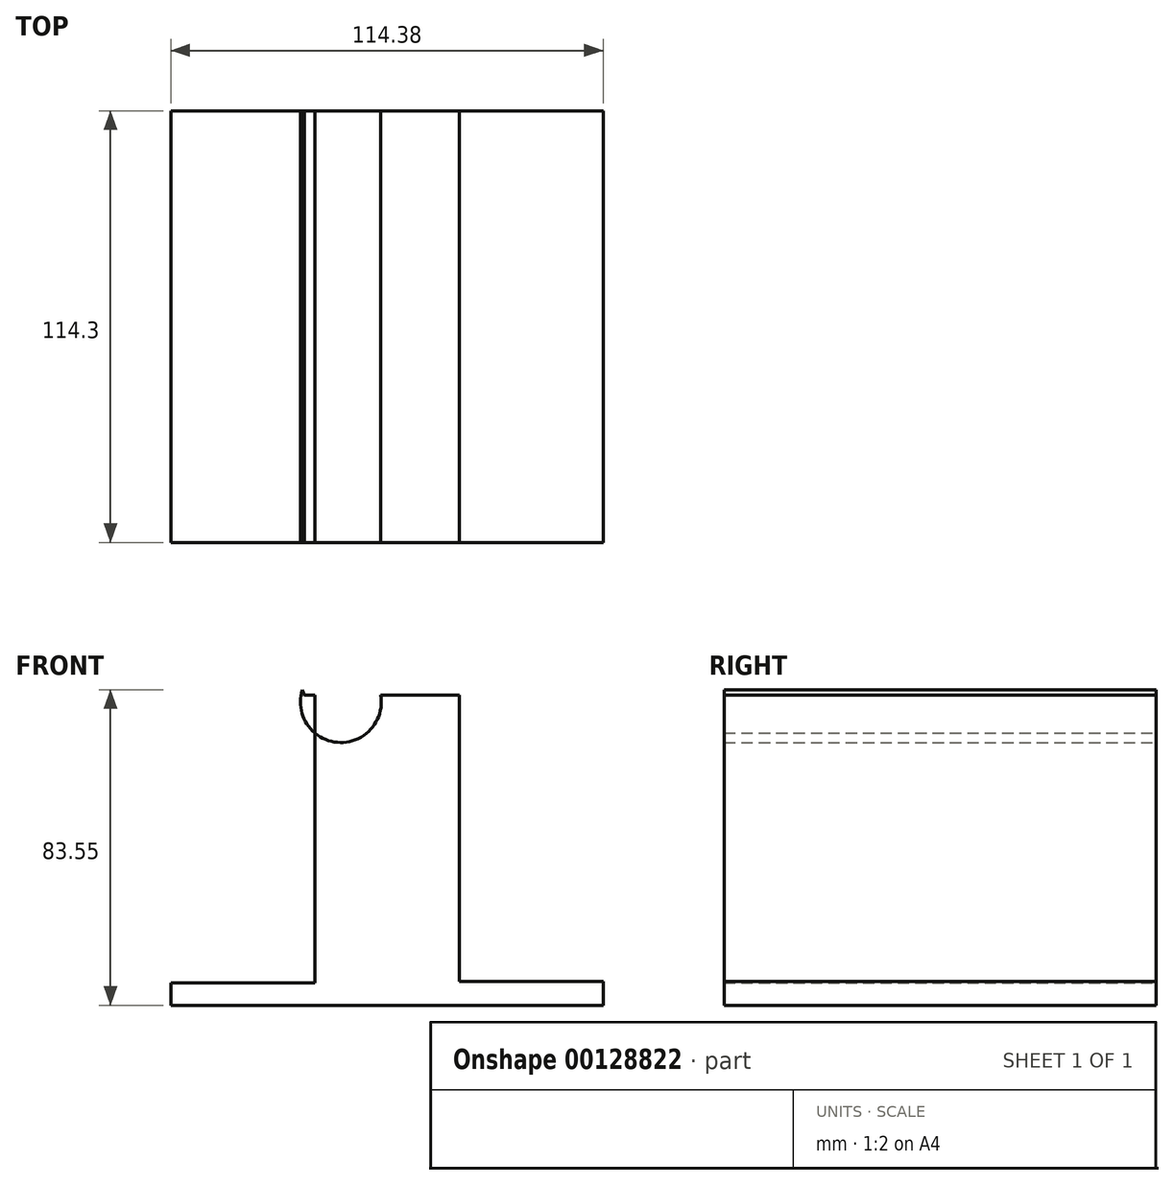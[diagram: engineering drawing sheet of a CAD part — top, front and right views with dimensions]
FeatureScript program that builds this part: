
annotation { "Feature Type Name" : "Feature", "Feature Type Description" : "" }
export const myFeature = defineFeature(function(context is Context, id is Id, definition is map)
    precondition{}
    {
        {
            var Q0;
            Q0=qCreatedBy(makeId("Front.planeOp"),FACE);
            var sketch = newSketch(context, id + "F0", { "sketchPlane" : qUnion([Q0])});
            skLineSegment(sketch, "E0", {"start": v(0, 0) * mm, "end": v(0, 5.88) * mm});
            skLineSegment(sketch, "E1", {"start": v(0, 5.88) * mm, "end": v(38.1, 5.88) * mm});
            skLineSegment(sketch, "E2", {"start": v(38.1, 5.88) * mm, "end": v(38.1, 82.08) * mm});
            skLineSegment(sketch, "E3", {"start": v(76.28, 82.08) * mm, "end": v(76.28, 49.35) * mm});
            skLineSegment(sketch, "E4", {"start": v(76.28, 6.25) * mm, "end": v(114.38, 6.25) * mm});
            skLineSegment(sketch, "E5", {"start": v(114.38, 6.25) * mm, "end": v(114.38, 0) * mm});
            skLineSegment(sketch, "E6", {"start": v(114.38, 0) * mm, "end": v(0, 0) * mm});
            skArc(sketch, "E7", {"start": v(35.3, 82.08) * mm, "mid": v(35.07, 82.82) * mm, "end": v(34.8, 83.55) * mm});
            skLineSegment(sketch, "E8", {"start": v(35.3, 82.08) * mm, "end": v(38.1, 82.08) * mm});
            skLineSegment(sketch, "E9", {"start": v(76.28, 82.08) * mm, "end": v(55.52, 82.08) * mm});
            skArc(sketch, "E10", {"start": v(34.8, 83.55) * mm, "mid": v(44.23, 69.6) * mm, "end": v(55.52, 82.08) * mm});
            skLineSegment(sketch, "E11", {"start": v(76.28, 49.35) * mm, "end": v(76.28, 6.25) * mm});
            skLineSegment(sketch, "E12", {"start": v(76.28, 64.02) * mm, "end": v(77.93, 64.41) * mm});
            skSolve(sketch);
        }
        {
            var Q0;
            Q0 = qSketchRegion(id + "F0", true);
            var Q1;
            Q1=makeQuery(id+"F0.imprint","IMPRINT",FACE,{"disambiguationData":[TD([[makeQuery(id+"F0.imprint","IMPRINT",EDGE,{"derivedFrom":sQuery(id+"F0.wireOp",EDGE,"E0")}),-1.0]])]});
            extrude(context, id + "F1", {"entities" : qUnion([Q0, Q1]), "depth" : 114.3 * mm});
        }
    });
